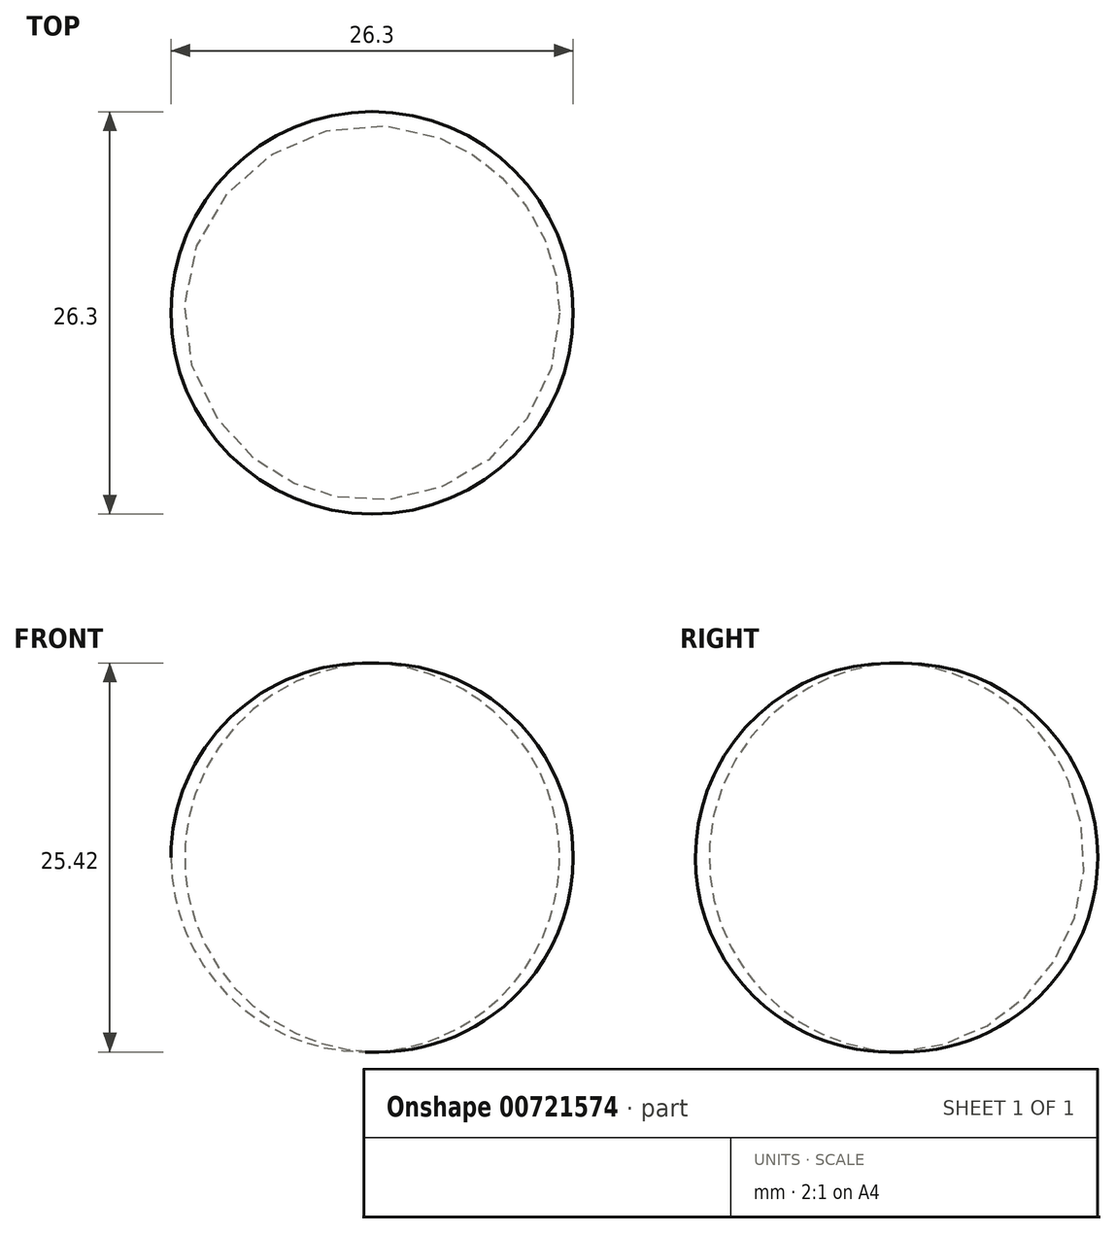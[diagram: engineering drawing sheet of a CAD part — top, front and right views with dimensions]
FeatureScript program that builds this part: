
annotation { "Feature Type Name" : "Feature", "Feature Type Description" : "" }
export const myFeature = defineFeature(function(context is Context, id is Id, definition is map)
    precondition{}
    {
        {
            var Q0;
            Q0=qCreatedBy(makeId("Front.planeOp"),FACE);
            var sketch = newSketch(context, id + "F0", { "sketchPlane" : qUnion([Q0])});
            skLineSegment(sketch, "E0", {"start": v(0, 0) * mm, "end": v(0, 25.4) * mm});
            skArc(sketch, "E1", {"start": v(0, 0) * mm, "mid": v(12.26, 12.7) * mm, "end": v(0, 25.4) * mm});
            skSolve(sketch);
        }
        {
            var Q0;
            Q0=makeQuery(id+"F0.imprint","IMPRINT",FACE,{"disambiguationData":[TD([[makeQuery(id+"F0.imprint","IMPRINT",EDGE,{"derivedFrom":sQuery(id+"F0.wireOp",EDGE,"E0")}),-1.0]])]});
            var Q1;
            Q1=sQuery(id+"F0.wireOp",EDGE,"E0");
            revolve(context, id + "F1", {"surfaceOperationType" : NewSurfaceOperationType.NEW, "entities" : qUnion([Q0]), "axis" : qUnion([Q1]), "revolveType" : RevolveType.FULL});
        }
    });
